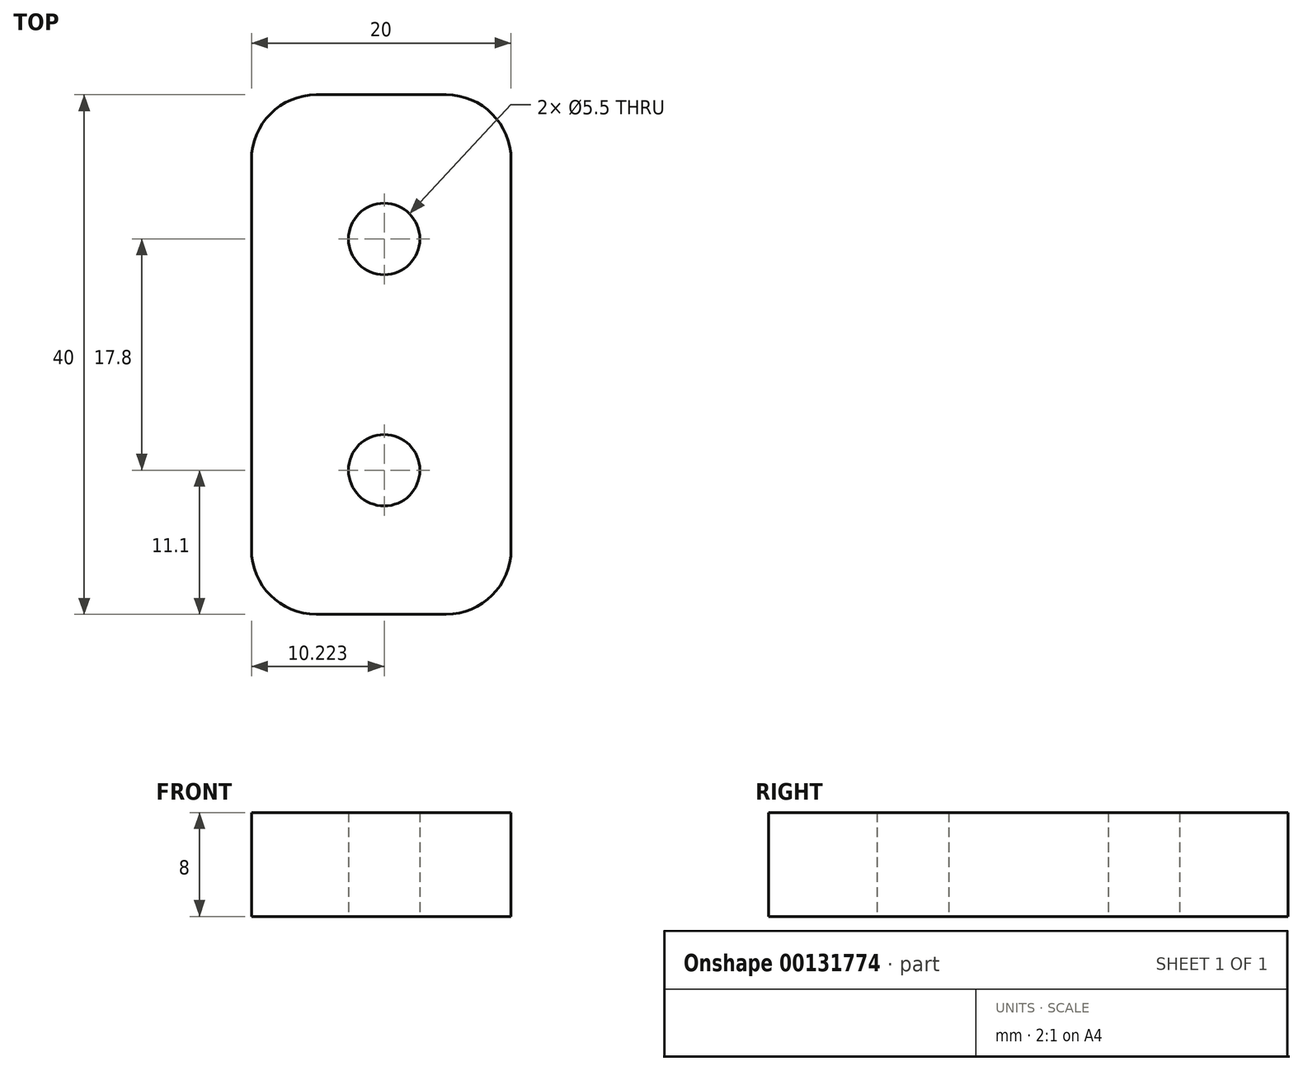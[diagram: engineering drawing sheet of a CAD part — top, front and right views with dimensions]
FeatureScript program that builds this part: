
annotation { "Feature Type Name" : "Feature", "Feature Type Description" : "" }
export const myFeature = defineFeature(function(context is Context, id is Id, definition is map)
    precondition{}
    {
        {
            var Q0;
            Q0=qCreatedBy(makeId("Top.planeOp"),FACE);
            var sketch = newSketch(context, id + "F0", { "sketchPlane" : qUnion([Q0])});
            skLineSegment(sketch, "E0.bottom", {"start": v(0, 0) * mm, "end": v(20, 0) * mm});
            skLineSegment(sketch, "E0.top", {"start": v(0, 40) * mm, "end": v(20, 40) * mm});
            skLineSegment(sketch, "E0.left", {"start": v(0, 0) * mm, "end": v(0, 40) * mm});
            skLineSegment(sketch, "E0.right", {"start": v(20, 0) * mm, "end": v(20, 40) * mm});
            skCircle(sketch, "E1", {"center": v(10.22, 28.9) * mm, "radius": 2.75 * mm});
            skCircle(sketch, "E2", {"center": v(10.22, 11.1) * mm, "radius": 2.75 * mm});
            skSolve(sketch);
        }
        {
            var Q0;
            Q0=makeQuery(id+"F0.imprint","IMPRINT",FACE,{"disambiguationData":[TD([[makeQuery(id+"F0.imprint","IMPRINT",EDGE,{"derivedFrom":sQuery(id+"F0.wireOp",EDGE,"E0.bottom")}),1.0]])]});
            extrude(context, id + "F1", {"entities" : qUnion([Q0]), "depth" : 8 * mm});
        }
        {
            var Q0;
            Q0=makeQuery(id+"F1.opExtrude","SWEPT_EDGE",EDGE,{"disambiguationData":[OSD([sQuery(id+"F0.wireOp",EDGE,"E0.bottom"),sQuery(id+"F0.wireOp",EDGE,"E0.left")])]});
            var Q1;
            Q1=makeQuery(id+"F1.opExtrude","SWEPT_EDGE",EDGE,{"disambiguationData":[OSD([sQuery(id+"F0.wireOp",EDGE,"E0.bottom"),sQuery(id+"F0.wireOp",EDGE,"E0.right")])]});
            var Q2;
            Q2=makeQuery(id+"F1.opExtrude","SWEPT_EDGE",EDGE,{"disambiguationData":[OSD([sQuery(id+"F0.wireOp",EDGE,"E0.top"),sQuery(id+"F0.wireOp",EDGE,"E0.left")])]});
            var Q3;
            Q3=makeQuery(id+"F1.opExtrude","SWEPT_EDGE",EDGE,{"disambiguationData":[OSD([sQuery(id+"F0.wireOp",EDGE,"E0.top"),sQuery(id+"F0.wireOp",EDGE,"E0.right")])]});
            fillet(context, id + "F2", {"entities" : qUnion([Q0, Q1, Q2, Q3]), "radius" : 5 * mm, "tangentPropagation" : true, "allowEdgeOverflow" : false});
        }
    });
